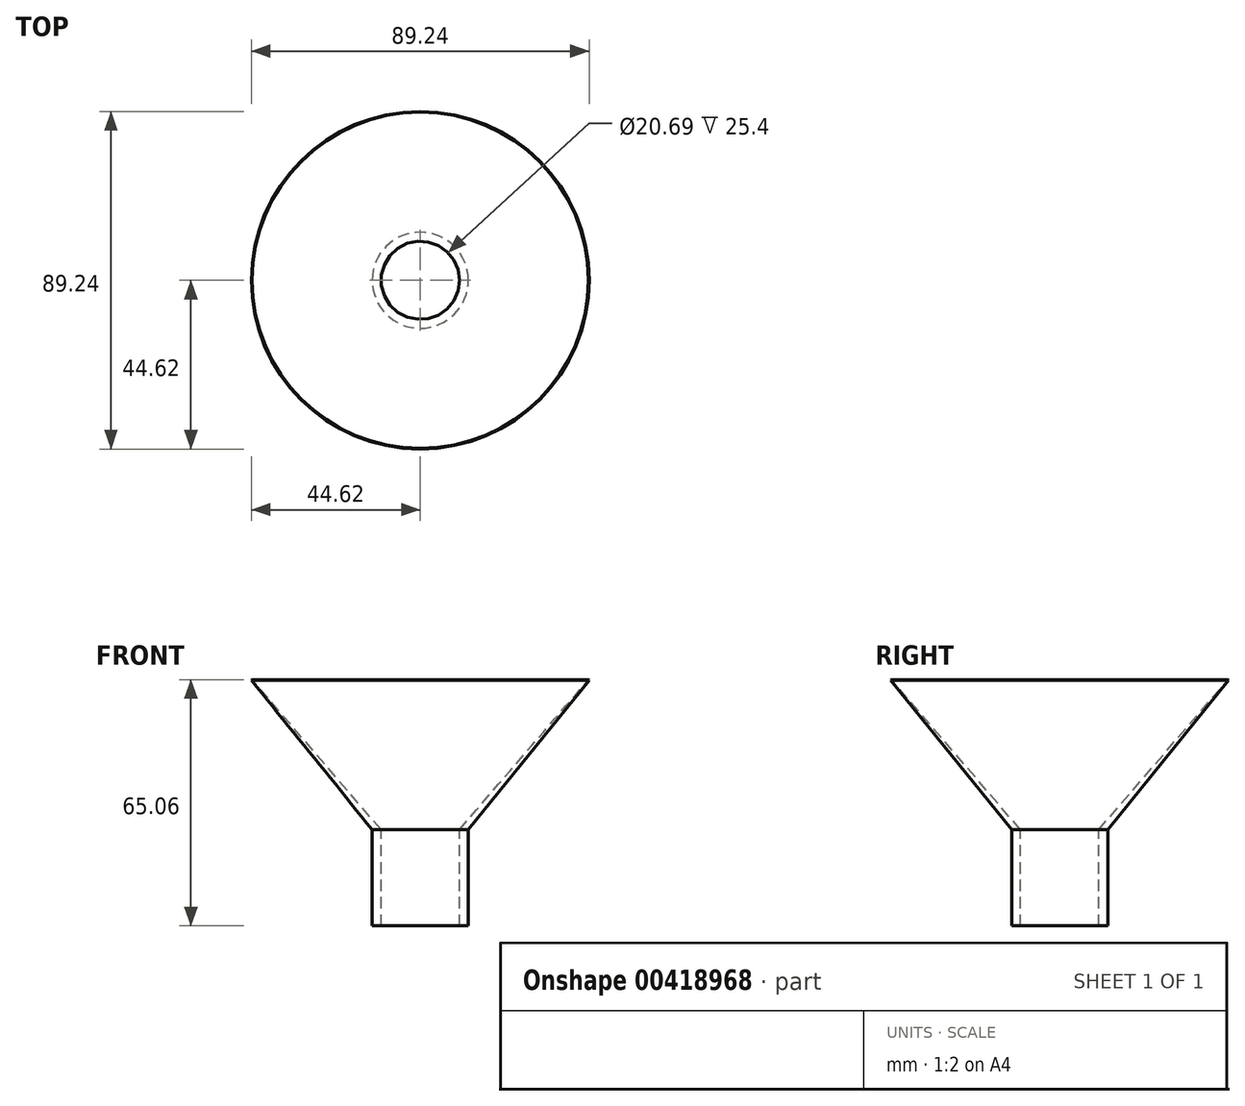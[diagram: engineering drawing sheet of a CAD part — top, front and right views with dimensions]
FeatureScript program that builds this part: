
annotation { "Feature Type Name" : "Feature", "Feature Type Description" : "" }
export const myFeature = defineFeature(function(context is Context, id is Id, definition is map)
    precondition{}
    {
        {
            var Q0;
            Q0=qCreatedBy(makeId("Front.planeOp"),FACE);
            var sketch = newSketch(context, id + "F0", { "sketchPlane" : qUnion([Q0])});
            skLineSegment(sketch, "E0", {"start": v(0, 0) * mm, "end": v(12.7, 0) * mm});
            skLineSegment(sketch, "E1", {"start": v(12.7, 0) * mm, "end": v(12.7, 25.4) * mm});
            skLineSegment(sketch, "E2", {"start": v(0, 0) * mm, "end": v(0, 25.4) * mm});
            skLineSegment(sketch, "E3", {"start": v(12.7, 25.4) * mm, "end": v(44.62, 64.92) * mm});
            skLineSegment(sketch, "E4", {"start": v(0, 25.4) * mm, "end": v(10.35, 25.4) * mm});
            skLineSegment(sketch, "E5", {"start": v(10.35, 25.4) * mm, "end": v(44.44, 65.06) * mm});
            skLineSegment(sketch, "E6", {"start": v(44.62, 64.92) * mm, "end": v(44.44, 65.06) * mm});
            skSolve(sketch);
        }
        {
            var Q0;
            Q0=makeQuery(id+"F0.imprint","IMPRINT",FACE,{"disambiguationData":[TD([[makeQuery(id+"F0.imprint","IMPRINT",EDGE,{"derivedFrom":sQuery(id+"F0.wireOp",EDGE,"E0")}),1.0]])]});
            var Q1;
            Q1=sQuery(id+"F0.wireOp",EDGE,"E2");
            revolve(context, id + "F1", {"entities" : qUnion([Q0]), "axis" : qUnion([Q1]), "revolveType" : RevolveType.FULL});
        }
        {
            var Q0;
            Q0=makeQuery(id+"F1.opRevolve","SWEPT_FACE",FACE,{"disambiguationData":[OSD([sQuery(id+"F0.wireOp",EDGE,"E4")])]});
            var sketch = newSketch(context, id + "F2", { "sketchPlane" : qUnion([Q0])});
            skCircle(sketch, "E7", {"center": v(0, 0) * mm, "radius": 10.34 * mm});
            skSolve(sketch);
        }
        {
            var Q0;
            Q0 = qSketchRegion(id + "F2", true);
            extrude(context, id + "F3", {"entities" : qUnion([Q0]), "operationType" : NewBodyOperationType.REMOVE, "oppositeDirection" : true, "depth" : 30.23 * mm});
        }
    });
